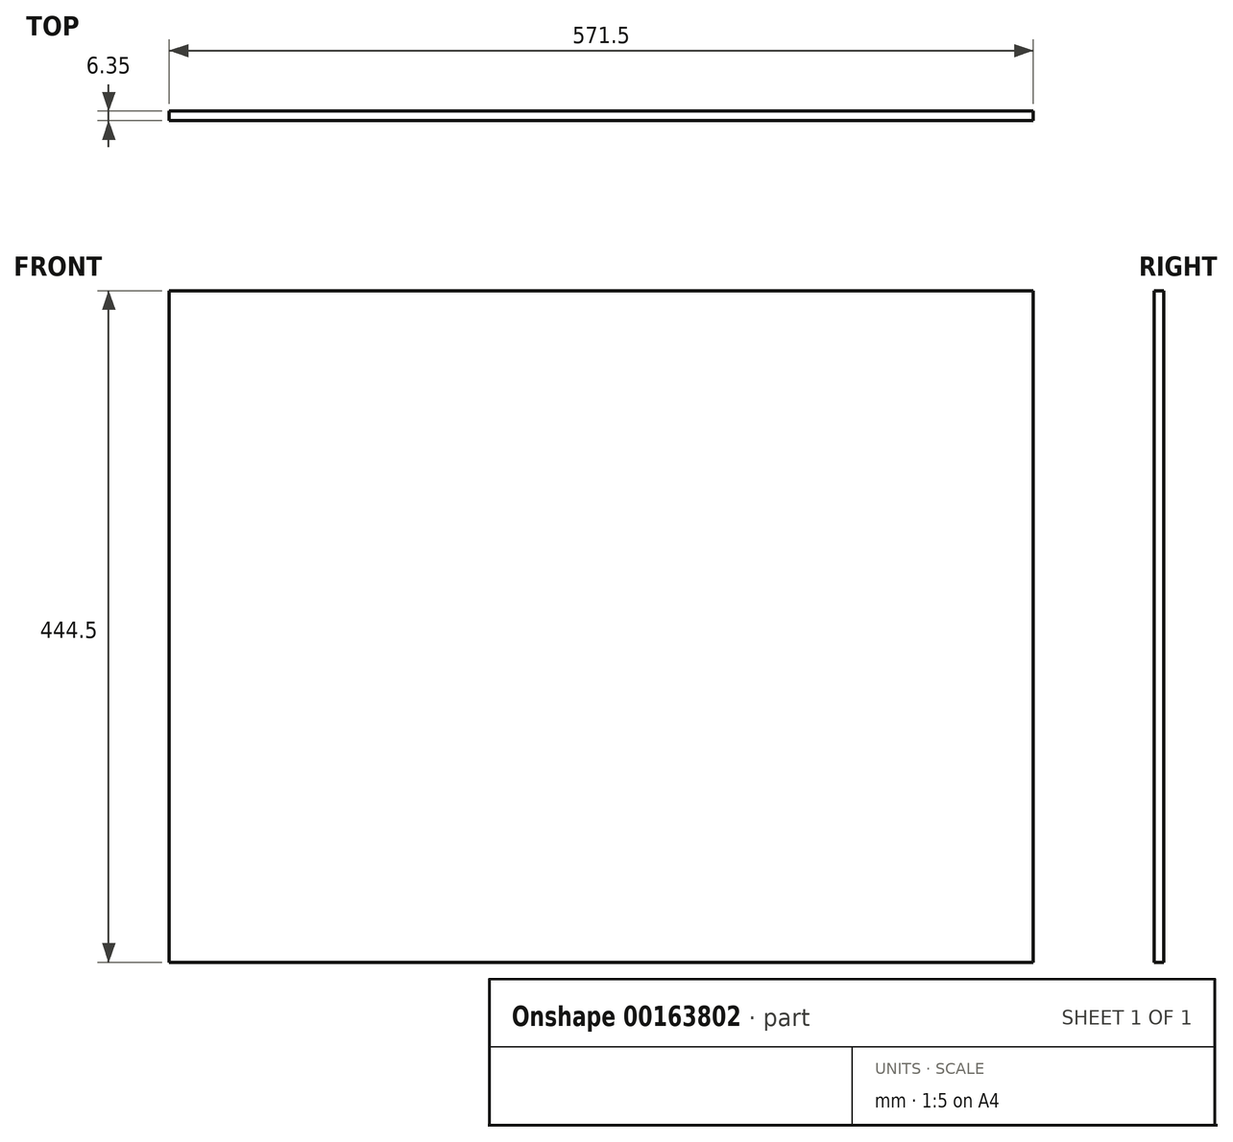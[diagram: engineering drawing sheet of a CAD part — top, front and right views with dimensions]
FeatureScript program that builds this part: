
annotation { "Feature Type Name" : "Feature", "Feature Type Description" : "" }
export const myFeature = defineFeature(function(context is Context, id is Id, definition is map)
    precondition{}
    {
        {
            var Q0;
            Q0=qCreatedBy(makeId("Front.planeOp"),FACE);
            var sketch = newSketch(context, id + "F0", { "sketchPlane" : qUnion([Q0])});
            skLineSegment(sketch, "E0.bottom", {"start": v(-285.75, -222.25) * mm, "end": v(285.75, -222.25) * mm});
            skLineSegment(sketch, "E0.top", {"start": v(-285.75, 222.25) * mm, "end": v(285.75, 222.25) * mm});
            skLineSegment(sketch, "E0.left", {"start": v(-285.75, -222.25) * mm, "end": v(-285.75, 222.25) * mm});
            skLineSegment(sketch, "E0.right", {"start": v(285.75, -222.25) * mm, "end": v(285.75, 222.25) * mm});
            skPoint(sketch, "E0.middle", {"position": v(0, 0) * mm});
            skSolve(sketch);
        }
        {
            var Q0;
            Q0=qSketchRegion(id+"F0",true);
            extrude(context, id + "F1", {"entities" : qUnion([Q0]), "depth" : 6.35 * mm});
        }
    });
